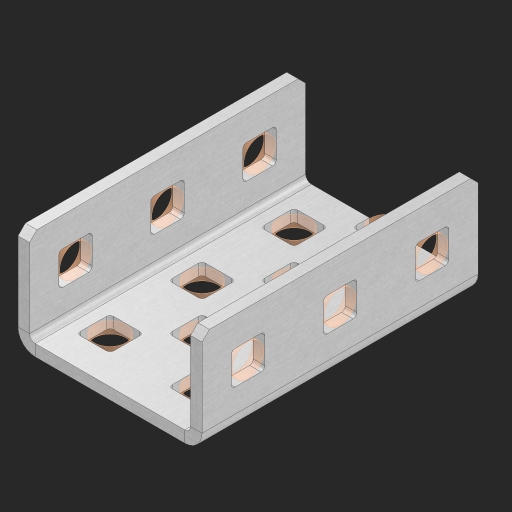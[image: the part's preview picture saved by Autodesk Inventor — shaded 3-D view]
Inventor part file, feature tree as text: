
AUTODESK INVENTOR PART (.ipt)
format: ipt  version: 2023 (Build 270158000, 158)  size: 621,568 bytes
history: native  units: in
note: dims shown in document units (in); Inventor stores cm internally (conversion verified against a paired STEP export)
features: other x22, extrude x13, sheet_metal_op x11, sketch x10, pattern_linear x2, mirror x1, chamfer x1
ambient origin geometry x8: Origin, YZ Plane, XZ Plane, XY Plane, X Axis, Y Axis, Z Axis, Center Point
bodies: Solid1 (feature_tree), Body (feature_tree)
feature tree (60):
  sheet_metal_op  "Flanges"
  other  "Flange Pattern Plane"
  other  "Flange Pattern Sketch"
  sheet_metal_op  "Flange Pattern"
  sheet_metal_op  "Body Pattern"
  pattern_linear  "Center Pattern"  Spacing1=0.0625in  [1 undecoded]
  other  "Arc Length"
  mirror  "Notch Mirror"
  pattern_linear  "Notch Pattern"  Spacing1=0.182in  [1 undecoded]
  chamfer  "End Chamfer"
  extrude  "Half Cut"  Depth=0.02in
  sketch  "Sketch1"  dims[d0=1.0in]
  other  "Plate1"
  sketch  "Sketch2"  dims[d1=1.5in]
  other  "Plate2"
  sheet_metal_op  "Bend1"
  sheet_metal_op  "Corner1"
  sketch  "Sketch3"  dims[d2=0.0625in]
  sketch  "Sketch7"  dims[d3=0.0625in]
  other  "Srf1"
  other  "Srf2"
  sketch  "Sketch8"  dims[d4=0.0312in]
  sketch  "Sketch9"  dims[d5=0.125in]
  other  "Srf91"
  sheet_metal_op  "Body Pattern Sketch"
  other  "Srf92"
  sketch  "Sketch13"  dims[d6=0.0625in]
  sketch  "Sketch14"  dims[d7=0.5in d8=90.0deg d9=0.0312in]
  sketch  "Sketch15"  dims[d10=0.25in]
  sketch  "Sketch16"  dims[d11=0.0625in d12=0.0625in d16=0.182in d17=0.02in d18=0.0625in d19=0.0in d20=0.25in d21=0.25in d38=1.1811in d40=0.5in d41=0.7874in d43=1.0in d46=0.172in d47=1.0in d48=0.0in d49=0.182in d50=0.02in d51=0.25in d52=0.25in d53=0.0625in d54=0.0in d55=0.172in d56=1.0in d57=0.0in d58=0.25in d60=1.1811in d62=0.5in d63=0.7874in d65=0.5in d85=0.1473in d86=0.1782in d88=0.04in d89=0.0625in d90=0.0in d91=0.04in d92=0.0491in d95=2.5in d96=0.04in d97=0.25in d98=45.0deg d99=0.25in d100=0.5in d101=0.0in d102=2.497in d106=0.182in d107=0.02in d108=0.5in d109=0.5in d110=0.0625in d111=0.0in d112=0.172in d113=0.5in d114=0.0in d117=0.5in d118=0.5in d119=0.5in]
  other  "Srf786"
  other  "Srf823"
  other  "Srf824"
  other  "Srf825"
  other  "Srf826"
  other  "Srf856"
  other  "Srf857"
  other  "Srf858"
  other  "Srf859"
  other  "Srf889"
  other  "Srf890"
  sheet_metal_op  "Flange Stamp"
  sheet_metal_op  "Flange Circle"
  sheet_metal_op  "Body Stamp"
  sheet_metal_op  "Body Circle"
  other  "Center Stamp"
  other  "Center Circle"
  sheet_metal_op  "Notch"
  extrude  "ExtrusionSrf2"  Depth=0.0625in
  extrude  "ExtrusionSrf92"  TaperAngle=0.0deg  [1 undecoded]
  extrude  "ExtrusionSrf823"  Depth=0.25in
  extrude  "ExtrusionSrf824"  Depth=0.25in
  extrude  "ExtrusionSrf825"  Depth=0.5in
  extrude  "ExtrusionSrf826"  Depth=0.5in
  extrude  "ExtrusionSrf856"  Depth=1.0in TaperAngle=0.0deg
  extrude  "ExtrusionSrf857"  Depth=0.182in
  extrude  "ExtrusionSrf858"  Depth=0.02in
  extrude  "ExtrusionSrf859"  Depth=0.25in
  extrude  "ExtrusionSrf889"  Depth=0.25in
  extrude  "ExtrusionSrf890"  Depth=0.0625in
note: 3 required parameter values undecoded (feature->parameter linkage not recoverable at this tier; creation-order binding heuristic only, values carry confidence <= 0.55)
